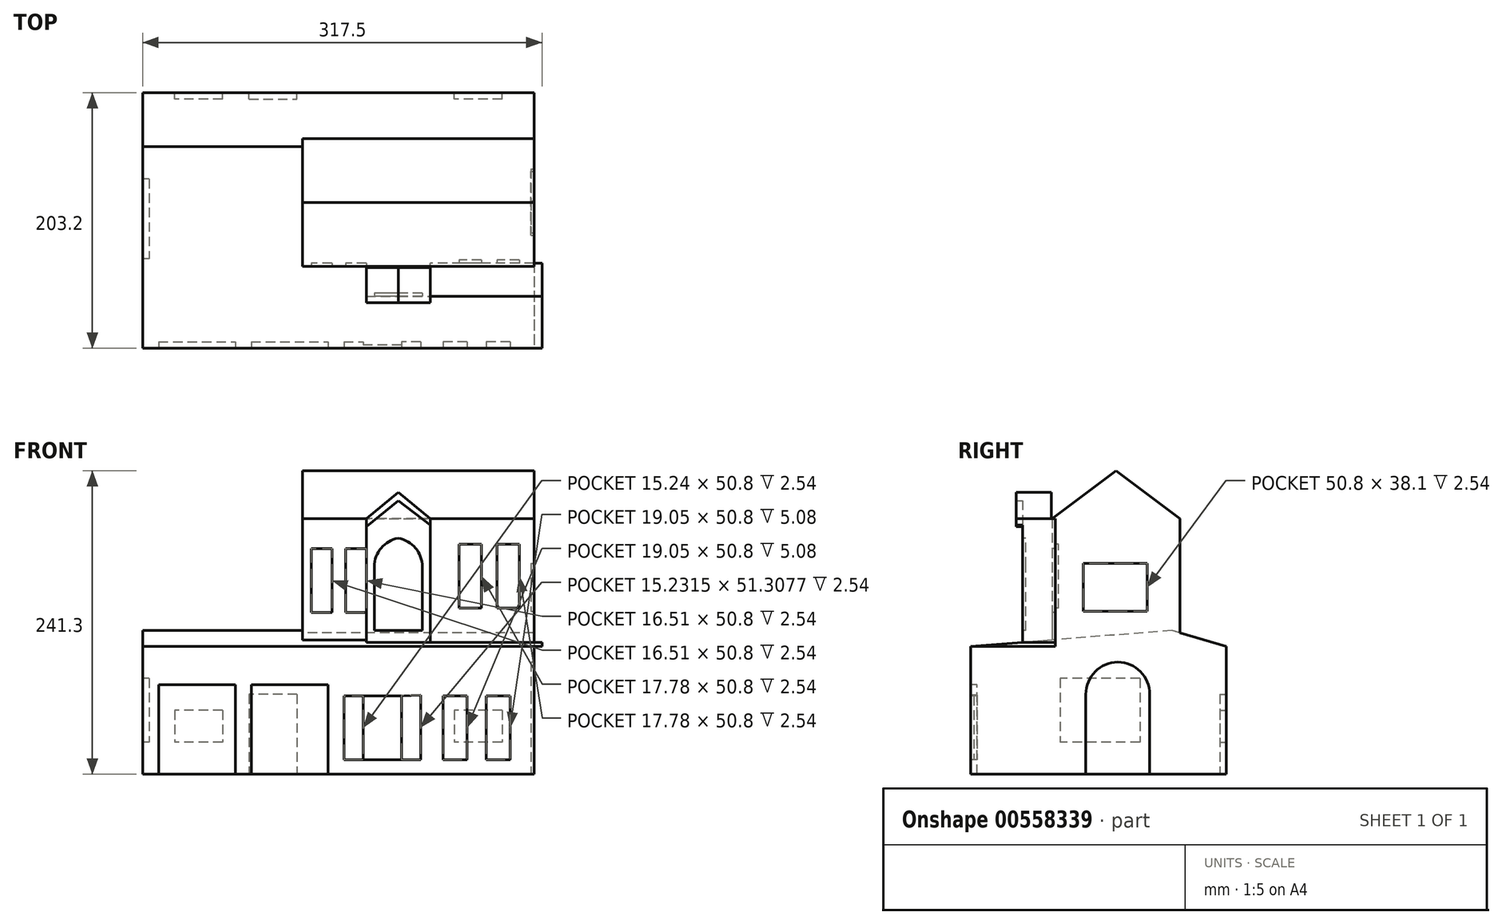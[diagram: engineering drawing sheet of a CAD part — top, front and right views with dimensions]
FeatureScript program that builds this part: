
annotation { "Feature Type Name" : "Feature", "Feature Type Description" : "" }
export const myFeature = defineFeature(function(context is Context, id is Id, definition is map)
    precondition{}
    {
        {
            var Q0;
            Q0=qCreatedBy(makeId("Front.planeOp"),FACE);
            var sketch = newSketch(context, id + "F0", { "sketchPlane" : qUnion([Q0])});
            skLineSegment(sketch, "E0.bottom", {"start": v(-177.8, 12.46) * mm, "end": v(127, 12.46) * mm});
            skLineSegment(sketch, "E0.top", {"start": v(-177.8, -89.14) * mm, "end": v(127, -89.14) * mm});
            skLineSegment(sketch, "E0.left", {"start": v(-177.8, 12.46) * mm, "end": v(-177.8, -89.14) * mm});
            skLineSegment(sketch, "E0.right", {"start": v(127, 12.46) * mm, "end": v(127, -89.14) * mm});
            skLineSegment(sketch, "E1", {"start": v(95.25, -77.71) * mm, "end": v(95.25, -26.91) * mm});
            skLineSegment(sketch, "E2", {"start": v(95.25, -26.91) * mm, "end": v(114.3, -26.91) * mm});
            skLineSegment(sketch, "E3", {"start": v(114.3, -26.91) * mm, "end": v(114.3, -77.71) * mm});
            skLineSegment(sketch, "E4", {"start": v(114.3, -77.71) * mm, "end": v(95.25, -77.71) * mm});
            skLineSegment(sketch, "E5", {"start": v(80, -26.91) * mm, "end": v(60.95, -26.91) * mm});
            skLineSegment(sketch, "E6", {"start": v(60.95, -26.91) * mm, "end": v(60.95, -77.71) * mm});
            skLineSegment(sketch, "E7", {"start": v(60.95, -77.71) * mm, "end": v(80, -77.71) * mm});
            skLineSegment(sketch, "E8", {"start": v(80, -77.71) * mm, "end": v(80, -26.91) * mm});
            skLineSegment(sketch, "E9", {"start": v(-2.54, -26.91) * mm, "end": v(-2.54, -77.71) * mm});
            skLineSegment(sketch, "E10", {"start": v(-2.54, -77.71) * mm, "end": v(27.94, -77.71) * mm});
            skLineSegment(sketch, "E11", {"start": v(27.94, -77.71) * mm, "end": v(27.94, -26.91) * mm});
            skLineSegment(sketch, "E12", {"start": v(27.94, -26.91) * mm, "end": v(-2.54, -26.91) * mm});
            skLineSegment(sketch, "E13", {"start": v(27.94, -77.71) * mm, "end": v(43.17, -77.71) * mm});
            skLineSegment(sketch, "E14", {"start": v(43.17, -77.71) * mm, "end": v(43.17, -26.4) * mm});
            skLineSegment(sketch, "E15", {"start": v(43.17, -26.4) * mm, "end": v(27.94, -26.91) * mm});
            skLineSegment(sketch, "E16", {"start": v(-2.54, -77.71) * mm, "end": v(-17.78, -77.71) * mm});
            skLineSegment(sketch, "E17", {"start": v(-17.78, -77.71) * mm, "end": v(-17.78, -26.91) * mm});
            skLineSegment(sketch, "E18", {"start": v(-17.78, -26.91) * mm, "end": v(-2.54, -26.91) * mm});
            skLineSegment(sketch, "E19", {"start": v(-165.1, -89.14) * mm, "end": v(-165.1, -18.02) * mm});
            skLineSegment(sketch, "E20", {"start": v(-165.1, -18.02) * mm, "end": v(-104.14, -18.02) * mm});
            skLineSegment(sketch, "E21", {"start": v(-104.14, -18.02) * mm, "end": v(-104.14, -89.14) * mm});
            skLineSegment(sketch, "E22", {"start": v(-104.14, -89.14) * mm, "end": v(-165.1, -89.14) * mm});
            skLineSegment(sketch, "E23", {"start": v(-91.44, -89.14) * mm, "end": v(-91.44, -18.02) * mm});
            skLineSegment(sketch, "E24", {"start": v(-91.44, -18.02) * mm, "end": v(-30.48, -18.02) * mm});
            skLineSegment(sketch, "E25", {"start": v(-30.48, -18.02) * mm, "end": v(-30.48, -89.14) * mm});
            skPoint(sketch, "E25.endSnap0", {"position": v(-25.4, -89.14) * mm});
            skLineSegment(sketch, "E26", {"start": v(-30.48, -89.14) * mm, "end": v(-91.44, -89.14) * mm});
            skSolve(sketch);
        }
        {
            var Q0;
            Q0=makeQuery(id+"F0.imprint","IMPRINT",FACE,{"disambiguationData":[TD([[makeQuery(id+"F0.imprint","IMPRINT",EDGE,{"derivedFrom":sQuery(id+"F0.wireOp",EDGE,"E0.bottom")}),-1.0]])]});
            var Q1;
            Q1=makeQuery(id+"F0.imprint","IMPRINT",FACE,{"disambiguationData":[TD([[makeQuery(id+"F0.imprint","IMPRINT",EDGE,{"derivedFrom":sQuery(id+"F0.wireOp",EDGE,"E1")}),-1.0]])]});
            var Q2;
            Q2=makeQuery(id+"F0.imprint","IMPRINT",FACE,{"disambiguationData":[TD([[makeQuery(id+"F0.imprint","IMPRINT",EDGE,{"derivedFrom":sQuery(id+"F0.wireOp",EDGE,"E5")}),1.0]])]});
            var Q3;
            Q3=makeQuery(id+"F0.imprint","IMPRINT",FACE,{"disambiguationData":[TD([[makeQuery(id+"F0.imprint","IMPRINT",EDGE,{"derivedFrom":sQuery(id+"F0.wireOp",EDGE,"E11")}),-1.0]])]});
            var Q4;
            Q4=makeQuery(id+"F0.imprint","IMPRINT",FACE,{"disambiguationData":[TD([[makeQuery(id+"F0.imprint","IMPRINT",EDGE,{"derivedFrom":sQuery(id+"F0.wireOp",EDGE,"E9")}),1.0]])]});
            var Q5;
            Q5=makeQuery(id+"F0.imprint","IMPRINT",FACE,{"disambiguationData":[TD([[makeQuery(id+"F0.imprint","IMPRINT",EDGE,{"derivedFrom":sQuery(id+"F0.wireOp",EDGE,"E9")}),-1.0]])]});
            var Q6;
            Q6=makeQuery(id+"F0.imprint","IMPRINT",FACE,{"disambiguationData":[TD([[makeQuery(id+"F0.imprint","IMPRINT",EDGE,{"derivedFrom":sQuery(id+"F0.wireOp",EDGE,"E23")}),-1.0]])]});
            var Q7;
            Q7=makeQuery(id+"F0.imprint","IMPRINT",FACE,{"disambiguationData":[TD([[makeQuery(id+"F0.imprint","IMPRINT",EDGE,{"derivedFrom":sQuery(id+"F0.wireOp",EDGE,"E19")}),-1.0]])]});
            extrude(context, id + "F1", {"entities" : qUnion([Q0, Q1, Q2, Q3, Q4, Q5, Q6, Q7]), "oppositeDirection" : true, "depth" : 203.2 * mm, "offsetDistance" : 25.4 * mm});
        }
        {
            var Q0;
            Q0=makeQuery(id+"F0.imprint","IMPRINT",FACE,{"disambiguationData":[TD([[makeQuery(id+"F0.imprint","IMPRINT",EDGE,{"derivedFrom":sQuery(id+"F0.wireOp",EDGE,"E9")}),-1.0]])]});
            var Q1;
            Q1=makeQuery(id+"F0.imprint","IMPRINT",FACE,{"disambiguationData":[TD([[makeQuery(id+"F0.imprint","IMPRINT",EDGE,{"derivedFrom":sQuery(id+"F0.wireOp",EDGE,"E11")}),-1.0]])]});
            var Q2;
            Q2=makeQuery(id+"F0.imprint","IMPRINT",FACE,{"disambiguationData":[TD([[makeQuery(id+"F0.imprint","IMPRINT",EDGE,{"derivedFrom":sQuery(id+"F0.wireOp",EDGE,"E5")}),1.0]])]});
            var Q3;
            Q3=makeQuery(id+"F0.imprint","IMPRINT",FACE,{"disambiguationData":[TD([[makeQuery(id+"F0.imprint","IMPRINT",EDGE,{"derivedFrom":sQuery(id+"F0.wireOp",EDGE,"E1")}),-1.0]])]});
            var Q4;
            Q4=makeQuery(id+"F0.imprint","IMPRINT",FACE,{"disambiguationData":[TD([[makeQuery(id+"F0.imprint","IMPRINT",EDGE,{"derivedFrom":sQuery(id+"F0.wireOp",EDGE,"E23")}),-1.0]])]});
            var Q5;
            Q5=makeQuery(id+"F0.imprint","IMPRINT",FACE,{"disambiguationData":[TD([[makeQuery(id+"F0.imprint","IMPRINT",EDGE,{"derivedFrom":sQuery(id+"F0.wireOp",EDGE,"E19")}),-1.0]])]});
            extrude(context, id + "F2", {"entities" : qUnion([Q0, Q1, Q2, Q3, Q4, Q5]), "operationType" : NewBodyOperationType.REMOVE, "oppositeDirection" : true, "depth" : 5.08 * mm, "offsetDistance" : 25.4 * mm});
        }
        {
            var Q0;
            Q0=makeQuery(id+"F0.imprint","IMPRINT",FACE,{"disambiguationData":[TD([[makeQuery(id+"F0.imprint","IMPRINT",EDGE,{"derivedFrom":sQuery(id+"F0.wireOp",EDGE,"E9")}),1.0]])]});
            extrude(context, id + "F3", {"entities" : qUnion([Q0]), "operationType" : NewBodyOperationType.REMOVE, "oppositeDirection" : true, "depth" : 2.54 * mm, "offsetDistance" : 25.4 * mm});
        }
        {
            var Q0;
            Q0=makeQuery(id+"F1.opExtrude","SWEPT_FACE",FACE,{"disambiguationData":[OSD([sQuery(id+"F0.wireOp",EDGE,"E0.left")])]});
            var sketch = newSketch(context, id + "F4", { "sketchPlane" : qUnion([Q0])});
            skLineSegment(sketch, "E27", {"start": v(-203.2, 12.46) * mm, "end": v(-160.24, 25.16) * mm});
            skLineSegment(sketch, "E28", {"start": v(-160.24, 25.16) * mm, "end": v(0, 12.46) * mm});
            skLineSegment(sketch, "E29", {"start": v(-203.2, 12.46) * mm, "end": v(0, 12.46) * mm});
            skSolve(sketch);
        }
        {
            var Q0;
            Q0=makeQuery(id+"F4.imprint","IMPRINT",FACE,{"disambiguationData":[TD([[makeQuery(id+"F4.imprint","IMPRINT",EDGE,{"derivedFrom":sQuery(id+"F4.wireOp",EDGE,"E27")}),-1.0]])]});
            extrude(context, id + "F5", {"entities" : qUnion([Q0]), "operationType" : NewBodyOperationType.ADD, "oppositeDirection" : true, "depth" : 127 * mm, "offsetDistance" : 25.4 * mm});
        }
        {
            var Q0;
            Q0=makeQuery(id+"F1.opExtrude","SWEPT_FACE",FACE,{"disambiguationData":[OSD([sQuery(id+"F0.wireOp",EDGE,"E0.bottom")])]});
            var sketch = newSketch(context, id + "F6", { "sketchPlane" : qUnion([Q0])});
            skLineSegment(sketch, "E30", {"start": v(-50.8, 64.94) * mm, "end": v(0, 64.94) * mm});
            skLineSegment(sketch, "E31", {"start": v(0, 64.94) * mm, "end": v(0, 38.86) * mm});
            skLineSegment(sketch, "E32", {"start": v(0, 38.86) * mm, "end": v(50.8, 38.86) * mm});
            skLineSegment(sketch, "E33", {"start": v(50.8, 38.86) * mm, "end": v(50.8, 64.94) * mm});
            skLineSegment(sketch, "E34", {"start": v(50.8, 64.94) * mm, "end": v(127, 64.94) * mm});
            skLineSegment(sketch, "E35", {"start": v(-50.8, 64.94) * mm, "end": v(-50.8, 166.54) * mm});
            skLineSegment(sketch, "E36", {"start": v(-50.8, 166.54) * mm, "end": v(127, 166.54) * mm});
            skLineSegment(sketch, "E37", {"start": v(127, 166.54) * mm, "end": v(127, 64.94) * mm});
            skSolve(sketch);
        }
        {
            var Q0;
            Q0=makeQuery(id+"F6.imprint","IMPRINT",FACE,{"disambiguationData":[TD([[makeQuery(id+"F6.imprint","IMPRINT",EDGE,{"derivedFrom":sQuery(id+"F6.wireOp",EDGE,"E30")}),1.0]])]});
            extrude(context, id + "F7", {"entities" : qUnion([Q0]), "operationType" : NewBodyOperationType.ADD, "depth" : 101.6 * mm, "offsetDistance" : 25.4 * mm});
        }
        {
            var Q0;
            Q0=makeQuery(id+"F7.opExtrude","SWEPT_FACE",FACE,{"disambiguationData":[OSD([sQuery(id+"F6.wireOp",EDGE,"E32")])]});
            var sketch = newSketch(context, id + "F8", { "sketchPlane" : qUnion([Q0])});
            skLineSegment(sketch, "E38", {"start": v(25.4, 114.06) * mm, "end": v(25.4, 134.96) * mm});
            skLineSegment(sketch, "E39", {"start": v(25.4, 134.96) * mm, "end": v(50.8, 114.06) * mm});
            skLineSegment(sketch, "E40", {"start": v(25.4, 134.96) * mm, "end": v(0, 114.06) * mm});
            skSolve(sketch);
        }
        {
            var Q0;
            Q0=makeQuery(id+"FgJlAHVsNRMwtT8_1.opExtrude","CAP_FACE",FACE,{"disambiguationData":[OSD([sQuery(id+"F6.wireOp",EDGE,"E32"),sQuery(id+"F8.wireOp",EDGE,"E39"),sQuery(id+"F8.wireOp",EDGE,"E40")])],"isStart":true});
            var Q1;
            {var subQ0=sQuery(id+"F0.wireOp",EDGE,"E0.right");Q1=makeQuery(id+"Fmxm7uohcpAgjp0_1.boolean.opBoolean","MERGE",FACE,{"derivedFrom":[makeQuery(id+"F7.boolean.opBoolean","MERGE",FACE,{"derivedFrom":[makeQuery(id+"F1.opExtrude","SWEPT_FACE",FACE,{"disambiguationData":[OSD([subQ0])]}),makeQuery(id+"F7.opExtrude","SWEPT_FACE",FACE,{"disambiguationData":[OSD([sQuery(id+"F6.wireOp",EDGE,"E37")])]})]}),makeQuery(id+"Fmxm7uohcpAgjp0_1.opExtrude","SWEPT_FACE",FACE,{"disambiguationData":[OSD([sQuery(id+"F0.wireOp",EDGE,"E0.bottom"),subQ0])]})]});}
            extrude(context, id + "F9", {"entities" : qUnion([Q0, Q1]), "operationType" : NewBodyOperationType.ADD, "depth" : 6.35 * mm, "offsetDistance" : 25.4 * mm});
        }
        {
            var Q0;
            {var subQ0=sQuery(id+"F8.wireOp",EDGE,"E38");Q0=makeQuery(id+"F8.imprint","IMPRINT",FACE,{"disambiguationData":[TD([[makeQuery(id+"F8.imprint","IMPRINT",EDGE,{"derivedFrom":subQ0}),1.0]])]});}
            var Q1;
            {var subQ0=sQuery(id+"F8.wireOp",EDGE,"E38");Q1=makeQuery(id+"F8.imprint","IMPRINT",FACE,{"disambiguationData":[TD([[makeQuery(id+"F8.imprint","IMPRINT",EDGE,{"derivedFrom":subQ0}),-1.0]])]});}
            extrude(context, id + "F10", {"entities" : qUnion([Q0, Q1]), "operationType" : NewBodyOperationType.ADD, "oppositeDirection" : true, "depth" : 25.4 * mm, "offsetDistance" : 25.4 * mm});
        }
        {
            var Q0;
            {var subQ1=sQuery(id+"F4.wireOp",EDGE,"E28");Q0=makeQuery(id+"F7.boolean.opBoolean","SPLIT",FACE,{"disambiguationData":[TD([makeQuery(id+"F5.opExtrude","SWEPT_FACE",FACE,{"disambiguationData":[OSD([subQ1])]})])],"derivedFrom":makeQuery(id+"F5.opExtrude","CAP_FACE",FACE,{"disambiguationData":[OSD([sQuery(id+"F4.wireOp",EDGE,"E27"),subQ1,sQuery(id+"F4.wireOp",EDGE,"E29")])],"isStart":false})});}
            var sketch = newSketch(context, id + "F11", { "sketchPlane" : qUnion([Q0])});
            skLineSegment(sketch, "E41", {"start": v(64.94, 17.6) * mm, "end": v(0, 12.46) * mm});
            skLineSegment(sketch, "E42", {"start": v(0, 12.46) * mm, "end": v(64.94, 12.46) * mm});
            skLineSegment(sketch, "E43", {"start": v(64.94, 12.46) * mm, "end": v(64.94, 17.6) * mm});
            skSolve(sketch);
        }
        {
            var Q0;
            Q0=makeQuery(id+"F7.opExtrude","SWEPT_FACE",FACE,{"disambiguationData":[OSD([sQuery(id+"F6.wireOp",EDGE,"E34")])]});
            var sketch = newSketch(context, id + "F12", { "sketchPlane" : qUnion([Q0])});
            skLineSegment(sketch, "E44", {"start": v(103.4, 39.6) * mm, "end": v(103.4, 90.38) * mm});
            skLineSegment(sketch, "E45", {"start": v(103.4, 90.38) * mm, "end": v(121.18, 90.38) * mm});
            skLineSegment(sketch, "E46", {"start": v(121.18, 90.38) * mm, "end": v(121.18, 40.02) * mm});
            skLineSegment(sketch, "E47", {"start": v(121.18, 40.02) * mm, "end": v(103.4, 39.6) * mm});
            skLineSegment(sketch, "E48", {"start": v(70.38, 90.4) * mm, "end": v(70.38, 39.6) * mm});
            skLineSegment(sketch, "E49", {"start": v(70.38, 39.6) * mm, "end": v(88.16, 39.6) * mm});
            skLineSegment(sketch, "E50", {"start": v(88.16, 39.6) * mm, "end": v(88.16, 90.4) * mm});
            skLineSegment(sketch, "E51", {"start": v(88.16, 90.4) * mm, "end": v(70.38, 90.4) * mm});
            skLineSegment(sketch, "E52", {"start": v(-43.87, 90.25) * mm, "end": v(-43.87, 39.45) * mm});
            skLineSegment(sketch, "E53", {"start": v(-43.87, 39.45) * mm, "end": v(-27.36, 39.45) * mm});
            skLineSegment(sketch, "E54", {"start": v(-27.36, 39.45) * mm, "end": v(-27.36, 90.25) * mm});
            skLineSegment(sketch, "E55", {"start": v(-27.36, 90.25) * mm, "end": v(-43.87, 90.25) * mm});
            skLineSegment(sketch, "E56", {"start": v(-16.51, 90.25) * mm, "end": v(-16.5, 39.45) * mm});
            skLineSegment(sketch, "E57", {"start": v(-16.5, 39.45) * mm, "end": v(0, 39.45) * mm});
            skLineSegment(sketch, "E58", {"start": v(0, 39.45) * mm, "end": v(0, 90.25) * mm});
            skLineSegment(sketch, "E59", {"start": v(0, 90.25) * mm, "end": v(-16.51, 90.25) * mm});
            skSolve(sketch);
        }
        {
            var Q0;
            Q0 = qSketchRegion(id + "F12", true);
            var Q1;
            Q1=makeQuery(id+"F7.opExtrude","SWEPT_FACE",FACE,{"disambiguationData":[OSD([sQuery(id+"F6.wireOp",EDGE,"E32")])]});
            extrude(context, id + "F13", {"entities" : qUnion([Q0, Q1]), "operationType" : NewBodyOperationType.REMOVE, "oppositeDirection" : true, "depth" : 2.54 * mm, "offsetDistance" : 25.4 * mm});
        }
        {
            var Q0;
            Q0=makeQuery(id+"F13.boolean.opBoolean","COPY",FACE,{"derivedFrom":makeQuery(id+"F13.opExtrude","CAP_FACE",FACE,{"disambiguationData":[OSD([sQuery(id+"F6.wireOp",EDGE,"E32")])],"isStart":false})});
            var sketch = newSketch(context, id + "F14", { "sketchPlane" : qUnion([Q0])});
            skLineSegment(sketch, "E60", {"start": v(6.35, 25.16) * mm, "end": v(6.35, 75.96) * mm});
            skLineSegment(sketch, "E61", {"start": v(6.35, 75.96) * mm, "end": v(44.45, 75.96) * mm});
            skLineSegment(sketch, "E62", {"start": v(44.45, 75.96) * mm, "end": v(44.45, 25.16) * mm});
            skLineSegment(sketch, "E63", {"start": v(44.45, 25.16) * mm, "end": v(6.35, 25.16) * mm});
            skArc(sketch, "E64", {"start": v(25.4, 98.5) * mm, "mid": v(11.75, 90.71) * mm, "end": v(6.35, 75.96) * mm});
            skArc(sketch, "E65", {"start": v(44.45, 75.96) * mm, "mid": v(39.05, 90.71) * mm, "end": v(25.4, 98.5) * mm});
            skSolve(sketch);
        }
        {
            var Q0;
            {var subQ3=sQuery(id+"F6.wireOp",EDGE,"E34");Q0=makeQuery(id+"FmhZTJAEbqoY8Ze_3.boolean.opBoolean","SPLIT",FACE,{"disambiguationData":[TD([makeQuery(id+"FmhZTJAEbqoY8Ze_3.opExtrude","SWEPT_FACE",FACE,{"disambiguationData":[OSD([sQuery(id+"Fv2lOEo5ZELkoC8_3.wireOp",EDGE,"OLnxfH1R-d0lU-qst8-CWAj-C3DLdYnxWyVM")])]})])],"derivedFrom":makeQuery(id+"F7.opExtrude","SWEPT_FACE",FACE,{"disambiguationData":[OSD([subQ3])]})});}
            var Q1;
            Q1=makeQuery(id+"F14.imprint","IMPRINT",FACE,{"disambiguationData":[TD([[makeQuery(id+"F14.imprint","IMPRINT",EDGE,{"derivedFrom":sQuery(id+"F14.wireOp",EDGE,"E60")}),-1.0]])]});
            var Q2;
            Q2=makeQuery(id+"F14.imprint","IMPRINT",FACE,{"disambiguationData":[TD([[makeQuery(id+"F14.imprint","IMPRINT",EDGE,{"derivedFrom":sQuery(id+"F14.wireOp",EDGE,"E61")}),1.0]])]});
            extrude(context, id + "F15", {"entities" : qUnion([Q0, Q1, Q2]), "operationType" : NewBodyOperationType.REMOVE, "oppositeDirection" : true, "depth" : 2.54 * mm, "offsetDistance" : 25.4 * mm});
        }
        {
            var Q0;
            Q0=makeQuery(id+"F7.opExtrude","SWEPT_FACE",FACE,{"disambiguationData":[OSD([sQuery(id+"F6.wireOp",EDGE,"E30")])]});
            var sketch = newSketch(context, id + "F16", { "sketchPlane" : qUnion([Q0])});
            skLineSegment(sketch, "E66", {"start": v(0, 114.06) * mm, "end": v(-50.8, 114.06) * mm});
            skLineSegment(sketch, "E67", {"start": v(-50.8, 114.06) * mm, "end": v(0, 114.06) * mm});
            skLineSegment(sketch, "E68", {"start": v(-50.8, 97.05) * mm, "end": v(-50.8, 114.06) * mm});
            skSolve(sketch);
        }
        {
            var Q0;
            Q0=makeQuery(id+"F15.boolean.opBoolean","MERGE",FACE,{"derivedFrom":[makeQuery(id+"F13.boolean.opBoolean","COPY",FACE,{"derivedFrom":makeQuery(id+"F13.opExtrude","CAP_FACE",FACE,{"disambiguationData":[OSD([sQuery(id+"F12.wireOp",EDGE,"E44"),sQuery(id+"F12.wireOp",EDGE,"E45"),sQuery(id+"F12.wireOp",EDGE,"E46"),sQuery(id+"F12.wireOp",EDGE,"E47")])],"isStart":false})}),makeQuery(id+"F13.boolean.opBoolean","COPY",FACE,{"derivedFrom":makeQuery(id+"F13.opExtrude","CAP_FACE",FACE,{"disambiguationData":[OSD([sQuery(id+"F12.wireOp",EDGE,"E48"),sQuery(id+"F12.wireOp",EDGE,"E49"),sQuery(id+"F12.wireOp",EDGE,"E50"),sQuery(id+"F12.wireOp",EDGE,"E51")])],"isStart":false})}),makeQuery(id+"F15.opExtrude","CAP_FACE",FACE,{"disambiguationData":[OSD([sQuery(id+"F0.wireOp",EDGE,"E0.bottom"),sQuery(id+"F0.wireOp",EDGE,"E0.right"),sQuery(id+"F6.wireOp",EDGE,"E34"),sQuery(id+"F6.wireOp",EDGE,"E37")])],"isStart":false})]});
            var sketch = newSketch(context, id + "F17", { "sketchPlane" : qUnion([Q0])});
            skLineSegment(sketch, "E69", {"start": v(103.88, 42.94) * mm, "end": v(103.88, 93.74) * mm});
            skLineSegment(sketch, "E70", {"start": v(103.88, 93.74) * mm, "end": v(121.66, 93.74) * mm});
            skLineSegment(sketch, "E71", {"start": v(121.66, 93.74) * mm, "end": v(121.66, 42.94) * mm});
            skLineSegment(sketch, "E72", {"start": v(121.66, 42.94) * mm, "end": v(103.88, 42.94) * mm});
            skLineSegment(sketch, "E73", {"start": v(73.68, 42.94) * mm, "end": v(73.68, 93.74) * mm});
            skLineSegment(sketch, "E74", {"start": v(73.68, 93.74) * mm, "end": v(91.46, 93.74) * mm});
            skLineSegment(sketch, "E75", {"start": v(91.46, 93.74) * mm, "end": v(91.46, 42.94) * mm});
            skLineSegment(sketch, "E76", {"start": v(91.46, 42.94) * mm, "end": v(73.68, 42.94) * mm});
            skSolve(sketch);
        }
        {
            var Q0;
            Q0=makeQuery(id+"F11.imprint","IMPRINT",FACE,{"disambiguationData":[TD([[makeQuery(id+"F11.imprint","IMPRINT",EDGE,{"derivedFrom":sQuery(id+"F11.wireOp",EDGE,"E41")}),1.0]])]});
            extrude(context, id + "F18", {"entities" : qUnion([Q0]), "operationType" : NewBodyOperationType.ADD, "depth" : 50.8 * mm, "offsetDistance" : 25.4 * mm});
        }
        {
            var Q0;
            Q0=makeQuery(id+"F18.opExtrude","CAP_FACE",FACE,{"disambiguationData":[OSD([sQuery(id+"F11.wireOp",EDGE,"E41"),sQuery(id+"F11.wireOp",EDGE,"E42"),sQuery(id+"F11.wireOp",EDGE,"E43")])],"isStart":false});
            var sketch = newSketch(context, id + "F19", { "sketchPlane" : qUnion([Q0])});
            skLineSegment(sketch, "E77", {"start": v(0, 12.46) * mm, "end": v(41.4, 15.74) * mm});
            skLineSegment(sketch, "E78", {"start": v(41.4, 15.74) * mm, "end": v(41.4, 12.46) * mm});
            skLineSegment(sketch, "E79", {"start": v(41.4, 12.46) * mm, "end": v(0, 12.46) * mm});
            skSolve(sketch);
        }
        {
            var Q0;
            Q0=makeQuery(id+"F19.imprint","IMPRINT",FACE,{"disambiguationData":[TD([[makeQuery(id+"F19.imprint","IMPRINT",EDGE,{"derivedFrom":sQuery(id+"F19.wireOp",EDGE,"E77")}),1.0]])]});
            extrude(context, id + "F20", {"entities" : qUnion([Q0]), "operationType" : NewBodyOperationType.ADD, "depth" : 50.8 * mm, "offsetDistance" : 25.4 * mm});
        }
        {
            var Q0;
            Q0=makeQuery(id+"F20.boolean.opBoolean","MERGE",FACE,{"derivedFrom":[makeQuery(id+"F7.opExtrude","SWEPT_FACE",FACE,{"disambiguationData":[OSD([sQuery(id+"F6.wireOp",EDGE,"E33")])]}),makeQuery(id+"F20.opExtrude","CAP_FACE",FACE,{"disambiguationData":[OSD([sQuery(id+"F19.wireOp",EDGE,"E77"),sQuery(id+"F19.wireOp",EDGE,"E78"),sQuery(id+"F19.wireOp",EDGE,"E79")])],"isStart":false})]});
            var sketch = newSketch(context, id + "F21", { "sketchPlane" : qUnion([Q0])});
            skLineSegment(sketch, "E80", {"start": v(0, 12.46) * mm, "end": v(41.4, 15.74) * mm});
            skLineSegment(sketch, "E81", {"start": v(41.4, 15.74) * mm, "end": v(67.48, 15.74) * mm});
            skLineSegment(sketch, "E82", {"start": v(67.48, 15.74) * mm, "end": v(67.48, 12.46) * mm});
            skLineSegment(sketch, "E83", {"start": v(0, 12.46) * mm, "end": v(67.48, 12.46) * mm});
            skSolve(sketch);
        }
        {
            var Q0;
            Q0=makeQuery(id+"F21.imprint","IMPRINT",FACE,{"disambiguationData":[TD([[makeQuery(id+"F21.imprint","IMPRINT",EDGE,{"derivedFrom":sQuery(id+"F21.wireOp",EDGE,"E80")}),1.0]])]});
            extrude(context, id + "F22", {"entities" : qUnion([Q0]), "operationType" : NewBodyOperationType.ADD, "depth" : 88.9 * mm, "offsetDistance" : 25.4 * mm});
        }
        {
            var Q0;
            Q0=makeQuery(id+"F17.imprint","IMPRINT",FACE,{"disambiguationData":[TD([[makeQuery(id+"F17.imprint","IMPRINT",EDGE,{"derivedFrom":sQuery(id+"F17.wireOp",EDGE,"E69")}),-1.0]])]});
            var Q1;
            Q1=makeQuery(id+"F17.imprint","IMPRINT",FACE,{"disambiguationData":[TD([[makeQuery(id+"F17.imprint","IMPRINT",EDGE,{"derivedFrom":sQuery(id+"F17.wireOp",EDGE,"E73")}),-1.0]])]});
            extrude(context, id + "F23", {"entities" : qUnion([Q0, Q1]), "operationType" : NewBodyOperationType.REMOVE, "oppositeDirection" : true, "depth" : 2.54 * mm, "offsetDistance" : 25.4 * mm});
        }
        {
            var Q0;
            Q0=makeQuery(id+"F13.boolean.opBoolean","COPY",FACE,{"derivedFrom":makeQuery(id+"F13.opExtrude","CAP_FACE",FACE,{"disambiguationData":[OSD([sQuery(id+"F6.wireOp",EDGE,"E32"),sQuery(id+"F8.wireOp",EDGE,"E39"),sQuery(id+"F8.wireOp",EDGE,"E40")])],"isStart":false})});
            var sketch = newSketch(context, id + "F24", { "sketchPlane" : qUnion([Q0])});
            skLineSegment(sketch, "E84", {"start": v(0, 107.77) * mm, "end": v(25.52, 128.48) * mm});
            skLineSegment(sketch, "E85", {"start": v(25.52, 128.48) * mm, "end": v(50.8, 109.12) * mm});
            skLineSegment(sketch, "E86", {"start": v(50.8, 109.12) * mm, "end": v(50.8, 114.06) * mm});
            skLineSegment(sketch, "E87", {"start": v(50.8, 114.06) * mm, "end": v(25.4, 134.96) * mm});
            skLineSegment(sketch, "E88", {"start": v(25.4, 134.96) * mm, "end": v(0, 114.06) * mm});
            skLineSegment(sketch, "E89", {"start": v(0, 114.06) * mm, "end": v(0, 107.77) * mm});
            skSolve(sketch);
        }
        {
            var Q0;
            Q0 = qSketchRegion(id + "F24", true);
            extrude(context, id + "F25", {"entities" : qUnion([Q0]), "operationType" : NewBodyOperationType.ADD, "depth" : 5.08 * mm, "offsetDistance" : 25.4 * mm});
        }
        {
            var Q0;
            Q0=makeQuery(id+"F5.boolean.opBoolean","MERGE",FACE,{"derivedFrom":[makeQuery(id+"F1.opExtrude","SWEPT_FACE",FACE,{"disambiguationData":[OSD([sQuery(id+"F0.wireOp",EDGE,"E0.left")])]}),makeQuery(id+"F5.opExtrude","CAP_FACE",FACE,{"disambiguationData":[OSD([sQuery(id+"F4.wireOp",EDGE,"E27"),sQuery(id+"F4.wireOp",EDGE,"E28"),sQuery(id+"F4.wireOp",EDGE,"E29")])],"isStart":true})]});
            var sketch = newSketch(context, id + "F26", { "sketchPlane" : qUnion([Q0])});
            skLineSegment(sketch, "E90.bottom", {"start": v(-134.62, -12.94) * mm, "end": v(-71.12, -12.94) * mm});
            skLineSegment(sketch, "E90.top", {"start": v(-134.62, -63.74) * mm, "end": v(-71.12, -63.74) * mm});
            skLineSegment(sketch, "E90.left", {"start": v(-134.62, -12.94) * mm, "end": v(-134.62, -63.74) * mm});
            skLineSegment(sketch, "E90.right", {"start": v(-71.12, -12.94) * mm, "end": v(-71.12, -63.74) * mm});
            skSolve(sketch);
        }
        {
            var Q0;
            Q0=makeQuery(id+"F26.imprint","IMPRINT",FACE,{"disambiguationData":[TD([[makeQuery(id+"F26.imprint","IMPRINT",EDGE,{"derivedFrom":sQuery(id+"F26.wireOp",EDGE,"E90.bottom")}),-1.0]])]});
            extrude(context, id + "F27", {"entities" : qUnion([Q0]), "operationType" : NewBodyOperationType.REMOVE, "oppositeDirection" : true, "depth" : 5.08 * mm, "offsetDistance" : 25.4 * mm});
        }
        {
            var Q0;
            Q0=makeQuery(id+"F9.opExtrude","CAP_FACE",FACE,{"disambiguationData":[OSD([sQuery(id+"F0.wireOp",EDGE,"E0.bottom"),sQuery(id+"F0.wireOp",EDGE,"E0.right"),sQuery(id+"F6.wireOp",EDGE,"E37")])],"isStart":false});
            var sketch = newSketch(context, id + "F28", { "sketchPlane" : qUnion([Q0])});
            skLineSegment(sketch, "E91.bottom", {"start": v(89.7, 78.61) * mm, "end": v(140.5, 78.61) * mm});
            skLineSegment(sketch, "E91.top", {"start": v(89.7, 40.51) * mm, "end": v(140.5, 40.51) * mm});
            skLineSegment(sketch, "E91.left", {"start": v(89.7, 78.61) * mm, "end": v(89.7, 40.51) * mm});
            skLineSegment(sketch, "E91.right", {"start": v(140.5, 78.61) * mm, "end": v(140.5, 40.51) * mm});
            skLineSegment(sketch, "E92.bottom", {"start": v(91.7, -25.64) * mm, "end": v(142.5, -25.64) * mm});
            skLineSegment(sketch, "E92.top", {"start": v(91.7, -89.14) * mm, "end": v(142.5, -89.14) * mm});
            skLineSegment(sketch, "E92.left", {"start": v(91.7, -25.64) * mm, "end": v(91.7, -89.14) * mm});
            skLineSegment(sketch, "E92.right", {"start": v(142.5, -25.64) * mm, "end": v(142.5, -89.14) * mm});
            skArc(sketch, "E93", {"start": v(117.1, 0) * mm, "mid": v(99.13, -7.6) * mm, "end": v(91.7, -25.64) * mm});
            skPoint(sketch, "E93.startSnap0", {"position": v(117.1, -25.64) * mm});
            skArc(sketch, "E94", {"start": v(142.5, -25.64) * mm, "mid": v(135.08, -7.6) * mm, "end": v(117.1, 0) * mm});
            skSolve(sketch);
        }
        {
            var Q0;
            Q0=makeQuery(id+"F28.imprint","IMPRINT",FACE,{"disambiguationData":[TD([[makeQuery(id+"F28.imprint","IMPRINT",EDGE,{"derivedFrom":sQuery(id+"F28.wireOp",EDGE,"E92.bottom")}),-1.0]])]});
            var Q1;
            Q1=makeQuery(id+"F28.imprint","IMPRINT",FACE,{"disambiguationData":[TD([[makeQuery(id+"F28.imprint","IMPRINT",EDGE,{"derivedFrom":sQuery(id+"F28.wireOp",EDGE,"E92.bottom")}),1.0]])]});
            var Q2;
            Q2=makeQuery(id+"F28.imprint","IMPRINT",FACE,{"disambiguationData":[TD([[makeQuery(id+"F28.imprint","IMPRINT",EDGE,{"derivedFrom":sQuery(id+"F28.wireOp",EDGE,"E91.bottom")}),-1.0]])]});
            extrude(context, id + "F29", {"entities" : qUnion([Q0, Q1, Q2]), "operationType" : NewBodyOperationType.REMOVE, "oppositeDirection" : true, "depth" : 2.54 * mm, "offsetDistance" : 25.4 * mm});
        }
        {
            var Q0;
            {var subQ0=sQuery(id+"F0.wireOp",EDGE,"E0.right");var subQ1=sQuery(id+"F0.wireOp",EDGE,"E0.bottom");Q0=makeQuery(id+"F9.boolean.opBoolean","MERGE",FACE,{"derivedFrom":[makeQuery(id+"Fmxm7uohcpAgjp0_1.boolean.opBoolean","MERGE",FACE,{"derivedFrom":[makeQuery(id+"F1.opExtrude","CAP_FACE",FACE,{"disambiguationData":[OSD([subQ1,sQuery(id+"F0.wireOp",EDGE,"E0.top"),sQuery(id+"F0.wireOp",EDGE,"E0.left"),subQ0,sQuery(id+"F0.wireOp",EDGE,"E22"),sQuery(id+"F0.wireOp",EDGE,"E26")])],"isStart":false}),makeQuery(id+"Fmxm7uohcpAgjp0_1.opExtrude","SWEPT_FACE",FACE,{"disambiguationData":[OSD([subQ1])]})]}),makeQuery(id+"F9.opExtrude","SWEPT_FACE",FACE,{"disambiguationData":[OSD([subQ1,subQ0]),TDD([makeQuery(id+"Fmxm7uohcpAgjp0_1.boolean.opBoolean","MERGE",EDGE,{"derivedFrom":[makeQuery(id+"F1.opExtrude","CAP_EDGE",EDGE,{"disambiguationData":[OSD([subQ0])],"isStart":false}),makeQuery(id+"Fmxm7uohcpAgjp0_1.opExtrude","SWEPT_EDGE",EDGE,{"disambiguationData":[OSD([subQ1,subQ0])]})]})])]})]});}
            var sketch = newSketch(context, id + "F30", { "sketchPlane" : qUnion([Q0])});
            skLineSegment(sketch, "E95.bottom", {"start": v(114.3, -38.34) * mm, "end": v(152.4, -38.34) * mm});
            skLineSegment(sketch, "E95.top", {"start": v(114.3, -63.74) * mm, "end": v(152.4, -63.74) * mm});
            skLineSegment(sketch, "E95.left", {"start": v(114.3, -38.34) * mm, "end": v(114.3, -63.74) * mm});
            skLineSegment(sketch, "E95.right", {"start": v(152.4, -38.34) * mm, "end": v(152.4, -63.74) * mm});
            skLineSegment(sketch, "E96.bottom", {"start": v(55.12, -25.64) * mm, "end": v(93.22, -25.64) * mm});
            skLineSegment(sketch, "E96.top", {"start": v(55.12, -89.14) * mm, "end": v(93.22, -89.14) * mm});
            skLineSegment(sketch, "E96.left", {"start": v(55.12, -25.64) * mm, "end": v(55.12, -89.14) * mm});
            skLineSegment(sketch, "E96.right", {"start": v(93.22, -25.64) * mm, "end": v(93.22, -89.14) * mm});
            skLineSegment(sketch, "E97.bottom", {"start": v(-107.95, -38.34) * mm, "end": v(-69.85, -38.34) * mm});
            skLineSegment(sketch, "E97.top", {"start": v(-107.95, -63.74) * mm, "end": v(-69.85, -63.74) * mm});
            skLineSegment(sketch, "E97.left", {"start": v(-107.95, -38.34) * mm, "end": v(-107.95, -63.74) * mm});
            skLineSegment(sketch, "E97.right", {"start": v(-69.85, -38.34) * mm, "end": v(-69.85, -63.74) * mm});
            skSolve(sketch);
        }
        {
            var Q0;
            Q0=makeQuery(id+"F30.imprint","IMPRINT",FACE,{"disambiguationData":[TD([[makeQuery(id+"F30.imprint","IMPRINT",EDGE,{"derivedFrom":sQuery(id+"F30.wireOp",EDGE,"E97.bottom")}),-1.0]])]});
            var Q1;
            Q1=makeQuery(id+"F30.imprint","IMPRINT",FACE,{"disambiguationData":[TD([[makeQuery(id+"F30.imprint","IMPRINT",EDGE,{"derivedFrom":sQuery(id+"F30.wireOp",EDGE,"E96.bottom")}),-1.0]])]});
            var Q2;
            Q2=makeQuery(id+"F30.imprint","IMPRINT",FACE,{"disambiguationData":[TD([[makeQuery(id+"F30.imprint","IMPRINT",EDGE,{"derivedFrom":sQuery(id+"F30.wireOp",EDGE,"E95.bottom")}),-1.0]])]});
            extrude(context, id + "F31", {"entities" : qUnion([Q0, Q1, Q2]), "operationType" : NewBodyOperationType.REMOVE, "oppositeDirection" : true, "depth" : 5.08 * mm, "offsetDistance" : 25.4 * mm});
        }
        {
            var Q0;
            {var subQ0=sQuery(id+"F4.wireOp",EDGE,"E27");Q0=makeQuery(id+"F7.boolean.opBoolean","SPLIT",FACE,{"disambiguationData":[TD([makeQuery(id+"F5.opExtrude","SWEPT_FACE",FACE,{"disambiguationData":[OSD([subQ0])]})])],"derivedFrom":makeQuery(id+"F5.opExtrude","CAP_FACE",FACE,{"disambiguationData":[OSD([subQ0,sQuery(id+"F4.wireOp",EDGE,"E28"),sQuery(id+"F4.wireOp",EDGE,"E29")])],"isStart":false})});}
            var sketch = newSketch(context, id + "F32", { "sketchPlane" : qUnion([Q0])});
            skLineSegment(sketch, "E98", {"start": v(166.54, 12.46) * mm, "end": v(166.54, 23.3) * mm});
            skLineSegment(sketch, "E99", {"start": v(166.54, 23.3) * mm, "end": v(203.2, 12.46) * mm});
            skLineSegment(sketch, "E100", {"start": v(203.2, 12.46) * mm, "end": v(166.54, 12.46) * mm});
            skSolve(sketch);
        }
        {
            var Q0;
            Q0=makeQuery(id+"F32.imprint","IMPRINT",FACE,{"disambiguationData":[TD([[makeQuery(id+"F32.imprint","IMPRINT",EDGE,{"derivedFrom":sQuery(id+"F32.wireOp",EDGE,"E98")}),1.0]])]});
            extrude(context, id + "F33", {"entities" : qUnion([Q0]), "operationType" : NewBodyOperationType.ADD, "depth" : 184.15 * mm, "offsetDistance" : 25.4 * mm});
        }
        {
            var Q0;
            Q0=makeQuery(id+"F7.opExtrude","SWEPT_FACE",FACE,{"disambiguationData":[OSD([sQuery(id+"F6.wireOp",EDGE,"E35")])]});
            var sketch = newSketch(context, id + "F34", { "sketchPlane" : qUnion([Q0])});
            skLineSegment(sketch, "E101", {"start": v(-166.54, 114.06) * mm, "end": v(-115.74, 152.16) * mm});
            skLineSegment(sketch, "E102", {"start": v(-115.74, 152.16) * mm, "end": v(-64.94, 114.06) * mm});
            skLineSegment(sketch, "E103", {"start": v(-64.94, 114.06) * mm, "end": v(-166.54, 114.06) * mm});
            skSolve(sketch);
        }
        {
            var Q0;
            Q0=makeQuery(id+"F34.imprint","IMPRINT",FACE,{"disambiguationData":[TD([[makeQuery(id+"F34.imprint","IMPRINT",EDGE,{"derivedFrom":sQuery(id+"F34.wireOp",EDGE,"E101")}),-1.0]])]});
            extrude(context, id + "F35", {"entities" : qUnion([Q0]), "operationType" : NewBodyOperationType.ADD, "oppositeDirection" : true, "depth" : 184.15 * mm, "offsetDistance" : 25.4 * mm});
        }
    });
